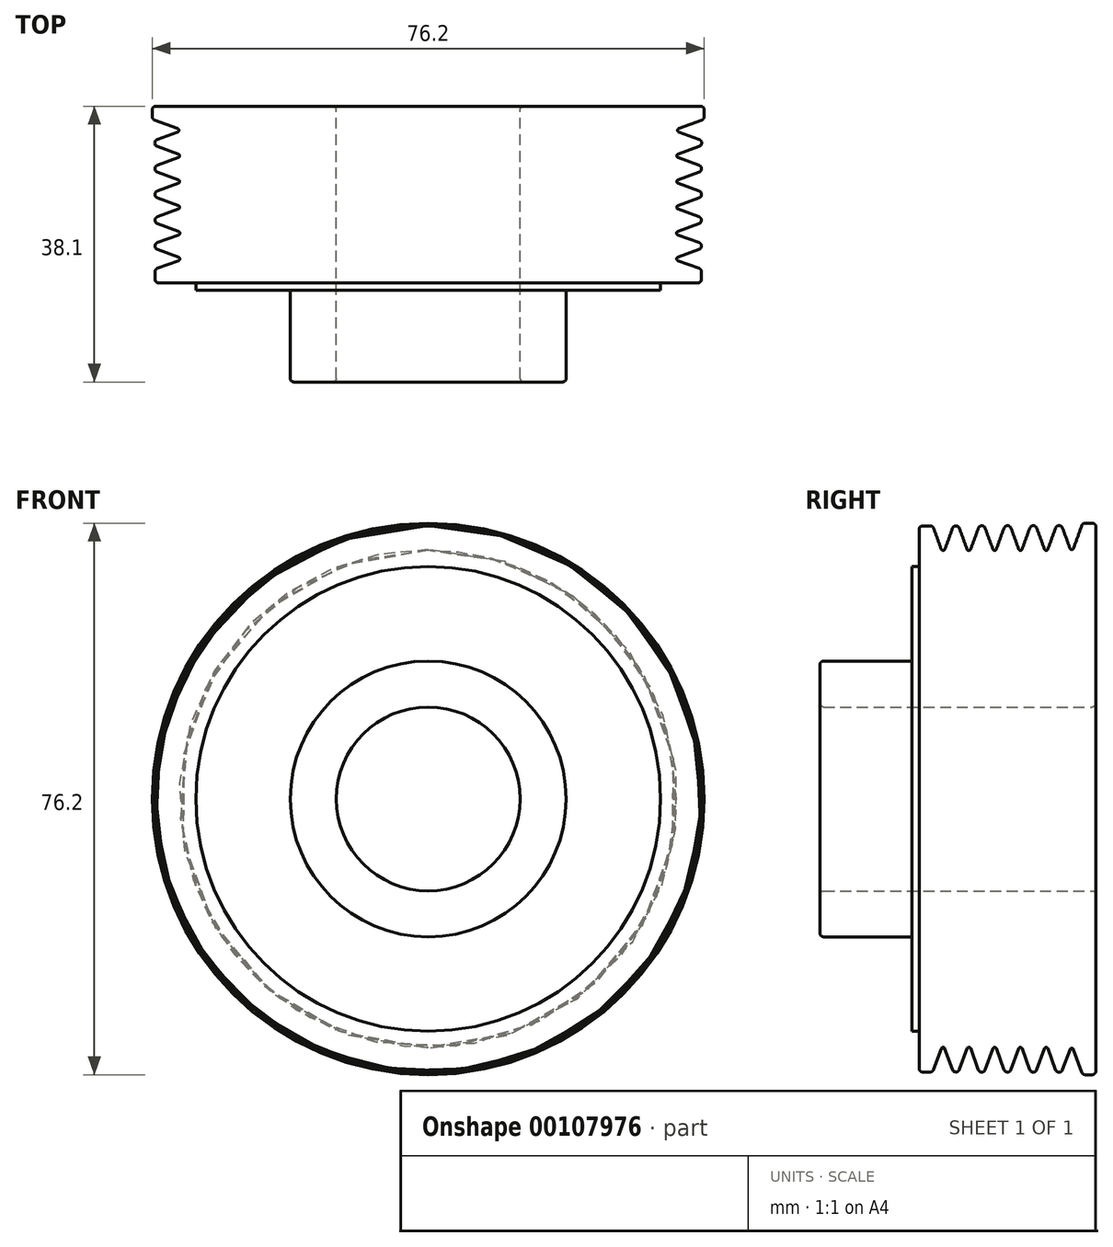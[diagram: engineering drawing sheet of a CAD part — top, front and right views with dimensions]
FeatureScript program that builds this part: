
annotation { "Feature Type Name" : "Feature", "Feature Type Description" : "" }
export const myFeature = defineFeature(function(context is Context, id is Id, definition is map)
    precondition{}
    {
        {
            var Q0;
            Q0=qCreatedBy(makeId("Front.planeOp"),FACE);
            var sketch = newSketch(context, id + "F0", { "sketchPlane" : qUnion([Q0])});
            skCircle(sketch, "E0", {"center": v(0, 0) * mm, "radius": 38.1 * mm});
            skCircle(sketch, "E1", {"center": v(0, 0) * mm, "radius": 12.7 * mm});
            skCircle(sketch, "E2", {"center": v(0, 0) * mm, "radius": 19.05 * mm});
            skCircle(sketch, "E3", {"center": v(0, 0) * mm, "radius": 32.1 * mm});
            skSolve(sketch);
        }
        {
            var Q0;
            Q0=qCreatedBy(makeId("Right.planeOp"),FACE);
            var sketch = newSketch(context, id + "F1", { "sketchPlane" : qUnion([Q0])});
            skLineSegment(sketch, "E4.bottom", {"start": v(0, 29.5) * mm, "end": v(-24.41, 29.5) * mm});
            skLineSegment(sketch, "E4.right", {"start": v(-24.41, 29.5) * mm, "end": v(-24.41, 37.72) * mm});
            skArc(sketch, "E5", {"start": v(-3.57, 34.6) * mm, "mid": v(-3.57, 34.58) * mm, "end": v(-3.56, 34.56) * mm});
            skLineSegment(sketch, "E6", {"start": v(-3.57, 34.6) * mm, "end": v(-4.6, 37.43) * mm});
            skLineSegment(sketch, "E7", {"start": v(-5.56, 37.43) * mm, "end": v(-6.63, 34.5) * mm});
            skArc(sketch, "E8", {"start": v(-4.6, 37.43) * mm, "mid": v(-5.08, 37.76) * mm, "end": v(-5.56, 37.43) * mm});
            skLineSegment(sketch, "E9", {"start": v(-7.1, 34.5) * mm, "end": v(-8.17, 37.41) * mm});
            skLineSegment(sketch, "E10", {"start": v(-9.12, 37.41) * mm, "end": v(-10.18, 34.5) * mm});
            skArc(sketch, "E11", {"start": v(-7.1, 34.5) * mm, "mid": v(-6.86, 34.32) * mm, "end": v(-6.63, 34.5) * mm});
            skArc(sketch, "E12", {"start": v(-10.66, 34.5) * mm, "mid": v(-10.42, 34.33) * mm, "end": v(-10.18, 34.5) * mm});
            skArc(sketch, "E13", {"start": v(-8.17, 37.41) * mm, "mid": v(-8.65, 37.74) * mm, "end": v(-9.12, 37.41) * mm});
            skLineSegment(sketch, "E14", {"start": v(-10.66, 34.5) * mm, "end": v(-11.72, 37.41) * mm});
            skLineSegment(sketch, "E15", {"start": v(-12.68, 37.41) * mm, "end": v(-13.74, 34.49) * mm});
            skArc(sketch, "E16", {"start": v(-11.72, 37.41) * mm, "mid": v(-12.2, 37.74) * mm, "end": v(-12.68, 37.41) * mm});
            skLineSegment(sketch, "E17", {"start": v(-10.66, 34.49) * mm, "end": v(-11.72, 37.41) * mm});
            skArc(sketch, "E18", {"start": v(-10.66, 34.49) * mm, "mid": v(-10.57, 34.37) * mm, "end": v(-10.42, 34.32) * mm});
            skArc(sketch, "E19", {"start": v(-14.22, 34.49) * mm, "mid": v(-13.98, 34.32) * mm, "end": v(-13.74, 34.49) * mm});
            skLineSegment(sketch, "E20", {"start": v(-14.22, 34.49) * mm, "end": v(-15.28, 37.4) * mm});
            skLineSegment(sketch, "E21", {"start": v(-16.23, 37.4) * mm, "end": v(-17.3, 34.47) * mm});
            skArc(sketch, "E22", {"start": v(-15.28, 37.4) * mm, "mid": v(-15.76, 37.74) * mm, "end": v(-16.23, 37.4) * mm});
            skLineSegment(sketch, "E23", {"start": v(-17.78, 34.47) * mm, "end": v(-18.84, 37.39) * mm});
            skLineSegment(sketch, "E24", {"start": v(-19.8, 37.39) * mm, "end": v(-20.86, 34.48) * mm});
            skArc(sketch, "E25", {"start": v(-17.78, 34.47) * mm, "mid": v(-17.54, 34.3) * mm, "end": v(-17.3, 34.47) * mm});
            skArc(sketch, "E26", {"start": v(-21.34, 34.48) * mm, "mid": v(-21.1, 34.3) * mm, "end": v(-20.86, 34.48) * mm});
            skArc(sketch, "E27", {"start": v(-18.84, 37.39) * mm, "mid": v(-19.32, 37.72) * mm, "end": v(-19.8, 37.39) * mm});
            skLineSegment(sketch, "E28", {"start": v(-21.34, 34.48) * mm, "end": v(-22.4, 37.4) * mm});
            skLineSegment(sketch, "E29", {"start": v(-24.41, 34.48) * mm, "end": v(-24.42, 34.47) * mm});
            skArc(sketch, "E30", {"start": v(-22.4, 37.4) * mm, "mid": v(-22.58, 37.63) * mm, "end": v(-22.88, 37.72) * mm});
            skLineSegment(sketch, "E31", {"start": v(-21.33, 34.47) * mm, "end": v(-22.4, 37.4) * mm});
            skArc(sketch, "E32", {"start": v(-21.33, 34.47) * mm, "mid": v(-21.24, 34.35) * mm, "end": v(-21.1, 34.3) * mm});
            skPoint(sketch, "E33.orphan", {"position": v(-3.56, 35.5) * mm});
            skPoint(sketch, "E34.orphan", {"position": v(-24.41, 35.5) * mm});
            skArc(sketch, "E35", {"start": v(-3.56, 34.56) * mm, "mid": v(-3.31, 34.43) * mm, "end": v(-3.1, 34.6) * mm});
            skLineSegment(sketch, "E36", {"start": v(-1.94, 37.77) * mm, "end": v(-3.1, 34.6) * mm});
            skLineSegment(sketch, "E37", {"start": v(-22.88, 37.72) * mm, "end": v(-24.41, 37.72) * mm});
            skArc(sketch, "E38", {"start": v(-1.52, 38.1) * mm, "mid": v(-1.78, 38) * mm, "end": v(-1.94, 37.77) * mm});
            skLineSegment(sketch, "E39", {"start": v(-1.52, 38.1) * mm, "end": v(0, 38.1) * mm});
            skLineSegment(sketch, "E40", {"start": v(0, 38.1) * mm, "end": v(0, 29.5) * mm});
            skPoint(sketch, "E41.orphan", {"position": v(-3.56, 29.5) * mm});
            skSolve(sketch);
        }
        {
            var Q0;
            Q0=makeQuery(id+"F1.imprint","IMPRINT",FACE,{"disambiguationData":[TD([[makeQuery(id+"F1.imprint","IMPRINT",EDGE,{"derivedFrom":sQuery(id+"F1.wireOp",EDGE,"E4.bottom")}),-1.0]])]});
            var Q1;
            Q1=sQuery(id+"F0.wireOp",EDGE,"E0");
            sweep(context, id + "F2", {"profiles" : qUnion([Q0]), "path" : qUnion([Q1])});
        }
        {
            var Q0;
            Q0=makeQuery(id+"F0.imprint","IMPRINT",FACE,{"disambiguationData":[TD([[makeQuery(id+"F0.imprint","IMPRINT",EDGE,{"derivedFrom":sQuery(id+"F0.wireOp",EDGE,"E1")}),-1.0]])]});
            extrude(context, id + "F3", {"entities" : qUnion([Q0]), "operationType" : NewBodyOperationType.ADD, "depth" : 38.1 * mm});
        }
        {
            var Q0;
            Q0=makeQuery(id+"F0.imprint","IMPRINT",FACE,{"disambiguationData":[TD([[makeQuery(id+"F0.imprint","IMPRINT",EDGE,{"derivedFrom":sQuery(id+"F0.wireOp",EDGE,"E2")}),-1.0]])]});
            extrude(context, id + "F4", {"entities" : qUnion([Q0]), "operationType" : NewBodyOperationType.ADD, "depth" : 25.4 * mm});
        }
        {
            var Q0;
            Q0=makeQuery(id+"F2.opSweep","SWEPT_FACE",FACE,{"disambiguationData":[OSD([sQuery(id+"F0.wireOp",EDGE,"E0"),sQuery(id+"F1.wireOp",EDGE,"E39")])]});
            var Q1;
            Q1=makeQuery(id+"F2.opSweep","SWEPT_EDGE",EDGE,{"disambiguationData":[OSD([sQuery(id+"F0.wireOp",EDGE,"E0"),sQuery(id+"F1.wireOp",EDGE,"E39"),sQuery(id+"F1.wireOp",EDGE,"E40")])]});
            var Q2;
            Q2=makeQuery(id+"F2.opSweep","SWEPT_FACE",FACE,{"disambiguationData":[OSD([sQuery(id+"F0.wireOp",EDGE,"E0"),sQuery(id+"F1.wireOp",EDGE,"E37")])]});
            var Q3;
            Q3=makeQuery(id+"F2.opSweep","SWEPT_EDGE",EDGE,{"disambiguationData":[OSD([sQuery(id+"F0.wireOp",EDGE,"E0"),sQuery(id+"F1.wireOp",EDGE,"E4.right"),sQuery(id+"F1.wireOp",EDGE,"E37")])]});
            var Q4;
            Q4=makeQuery(id+"F3.opExtrude","CAP_EDGE",EDGE,{"disambiguationData":[OSD([sQuery(id+"F0.wireOp",EDGE,"E0")])],"isStart":true});
            var Q5;
            Q5=makeQuery(id+"F2.opSweep","SWEPT_EDGE",EDGE,{"disambiguationData":[OSD([sQuery(id+"F0.wireOp",EDGE,"E0"),sQuery(id+"F1.wireOp",EDGE,"E4.bottom"),sQuery(id+"F1.wireOp",EDGE,"E40")])]});
            var Q6;
            Q6=makeQuery(id+"F2.opSweep","SWEPT_EDGE",EDGE,{"disambiguationData":[OSD([sQuery(id+"F0.wireOp",EDGE,"E0"),sQuery(id+"F1.wireOp",EDGE,"E4.bottom"),sQuery(id+"F1.wireOp",EDGE,"E4.right")])]});
            var Q7;
            Q7=makeQuery(id+"F3.opExtrude","CAP_EDGE",EDGE,{"disambiguationData":[OSD([sQuery(id+"F0.wireOp",EDGE,"E2")])],"isStart":false});
            var Q8;
            Q8=makeQuery(id+"F3.opExtrude","CAP_EDGE",EDGE,{"disambiguationData":[OSD([sQuery(id+"F0.wireOp",EDGE,"E1")])],"isStart":false});
            var Q9;
            Q9=makeQuery(id+"F3.opExtrude","CAP_EDGE",EDGE,{"disambiguationData":[OSD([sQuery(id+"F0.wireOp",EDGE,"E1")])],"isStart":true});
            fillet(context, id + "F5", {"entities" : qUnion([Q0, Q1, Q2, Q3, Q4, Q5, Q6, Q7, Q8, Q9]), "radius" : 0.5 * mm, "tangentPropagation" : true, "allowEdgeOverflow" : false});
        }
    });
